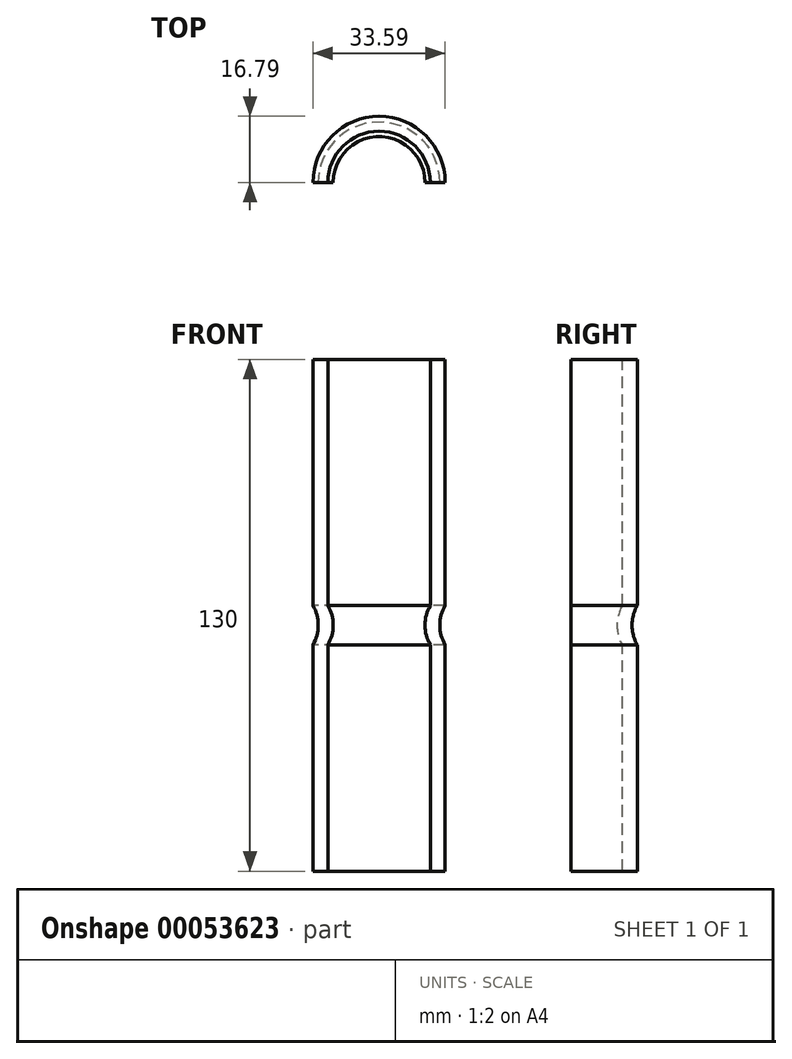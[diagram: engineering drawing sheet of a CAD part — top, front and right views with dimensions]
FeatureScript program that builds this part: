
annotation { "Feature Type Name" : "Feature", "Feature Type Description" : "" }
export const myFeature = defineFeature(function(context is Context, id is Id, definition is map)
    precondition{}
    {
        {
            var Q0;
            Q0=qCreatedBy(makeId("Front.planeOp"),FACE);
            var sketch = newSketch(context, id + "F0", { "sketchPlane" : qUnion([Q0])});
            skLineSegment(sketch, "E0", {"start": v(-43.46, 64.48) * mm, "end": v(-43.46, 1.98) * mm});
            skArc(sketch, "E1", {"start": v(-43.46, -8.02) * mm, "mid": v(-42.12, -3.02) * mm, "end": v(-43.46, 1.98) * mm});
            skLineSegment(sketch, "E2", {"start": v(-43.46, -8.02) * mm, "end": v(-43.46, -65.52) * mm});
            skLineSegment(sketch, "E3", {"start": v(-43.46, -65.52) * mm, "end": v(-39.67, -65.52) * mm});
            skLineSegment(sketch, "E4", {"start": v(-39.67, -65.52) * mm, "end": v(-39.67, -8.02) * mm});
            skArc(sketch, "E5", {"start": v(-39.67, -8.02) * mm, "mid": v(-38.33, -3.02) * mm, "end": v(-39.67, 1.98) * mm});
            skLineSegment(sketch, "E6", {"start": v(-39.67, 1.98) * mm, "end": v(-39.67, 64.48) * mm});
            skLineSegment(sketch, "E7", {"start": v(-39.67, 64.48) * mm, "end": v(-43.46, 64.48) * mm});
            skLineSegment(sketch, "E8", {"start": v(-26.67, 63.3) * mm, "end": v(-26.67, -66.7) * mm});
            skSolve(sketch);
        }
        {
            var Q0;
            Q0=makeQuery(id+"F0.imprint","IMPRINT",FACE,{"disambiguationData":[TD([[makeQuery(id+"F0.imprint","IMPRINT",EDGE,{"derivedFrom":sQuery(id+"F0.wireOp",EDGE,"E0")}),1.0]])]});
            var Q1;
            Q1=sQuery(id+"F0.wireOp",EDGE,"E8");
            revolve(context, id + "F1", {"entities" : qUnion([Q0]), "axis" : qUnion([Q1]), "revolveType" : RevolveType.ONE_DIRECTION, "angle" : 180 * degree});
        }
    });
